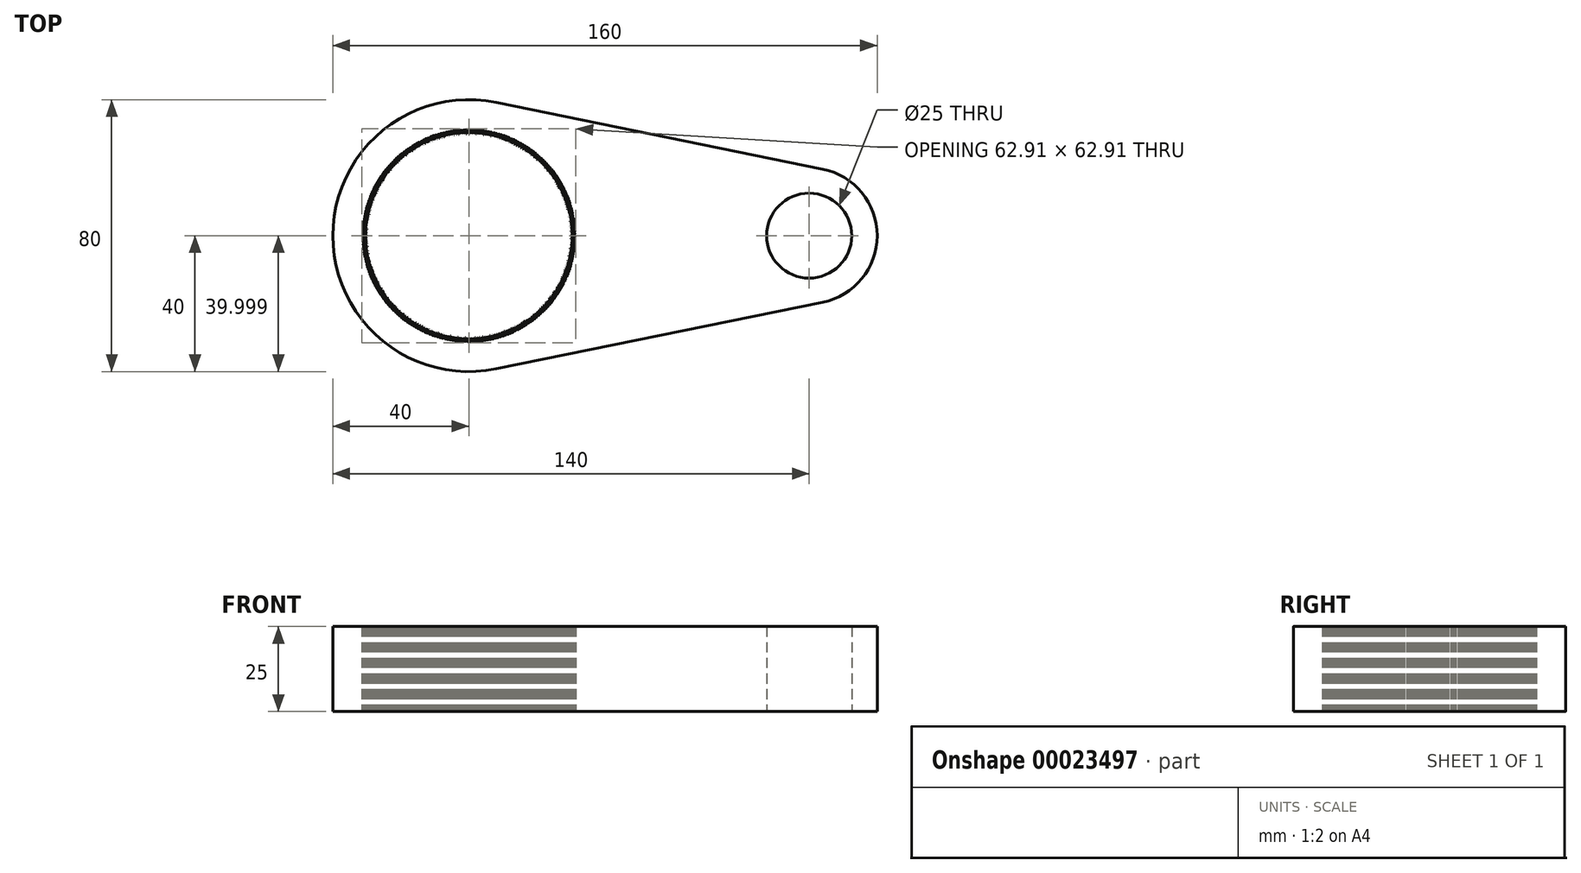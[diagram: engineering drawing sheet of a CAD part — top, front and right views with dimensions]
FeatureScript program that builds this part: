
annotation { "Feature Type Name" : "Feature", "Feature Type Description" : "" }
export const myFeature = defineFeature(function(context is Context, id is Id, definition is map)
    precondition{}
    {
        {
            var Q0;
            Q0=qCreatedBy(makeId("Top.planeOp"),FACE);
            var sketch = newSketch(context, id + "F0", { "sketchPlane" : qUnion([Q0])});
            skCircle(sketch, "E0", {"center": v(0, 0) * mm, "radius": 40 * mm});
            skCircle(sketch, "E1", {"center": v(100, 0) * mm, "radius": 20 * mm});
            skLineSegment(sketch, "E2", {"start": v(8, 39.2) * mm, "end": v(104, 19.6) * mm});
            skLineSegment(sketch, "E3", {"start": v(104, -19.6) * mm, "end": v(8, -39.2) * mm});
            skCircle(sketch, "E4", {"center": v(0, 0) * mm, "radius": 30 * mm});
            skCircle(sketch, "E5", {"center": v(100, 0) * mm, "radius": 12.5 * mm});
            skLineSegment(sketch, "E6", {"start": v(-21.76, -20.65) * mm, "end": v(-23.07, -21.39) * mm});
            skLineSegment(sketch, "E7", {"start": v(-23.07, -21.39) * mm, "end": v(-22.24, -20.14) * mm});
            skLineSegment(sketch, "E8.1.0", {"start": v(-22.25, -20.12) * mm, "end": v(-23.58, -20.82) * mm});
            skLineSegment(sketch, "E8.1.1", {"start": v(-23.58, -20.82) * mm, "end": v(-22.72, -19.6) * mm});
            skLineSegment(sketch, "E8.2.0", {"start": v(-22.74, -19.57) * mm, "end": v(-24.08, -20.24) * mm});
            skLineSegment(sketch, "E8.2.1", {"start": v(-24.08, -20.24) * mm, "end": v(-23.19, -19.04) * mm});
            skLineSegment(sketch, "E8.anchor1", {"start": v(0, 0) * mm, "end": v(-23.07, -21.39) * mm, "construction": true});
            skLineSegment(sketch, "E8.anchor2", {"start": v(0, 0) * mm, "end": v(-23.06, -21.4) * mm, "construction": true});
            skLineSegment(sketch, "E9.2.3.0", {"start": v(-23.2, -19.01) * mm, "end": v(-24.56, -19.65) * mm});
            skLineSegment(sketch, "E9.3.3.0", {"start": v(-24.56, -19.65) * mm, "end": v(-23.64, -18.47) * mm});
            skLineSegment(sketch, "E9.2.4.0", {"start": v(-23.66, -18.45) * mm, "end": v(-25.03, -19.05) * mm});
            skLineSegment(sketch, "E9.3.4.0", {"start": v(-25.03, -19.05) * mm, "end": v(-24.08, -17.89) * mm});
            skLineSegment(sketch, "E9.2.5.0", {"start": v(-24.1, -17.87) * mm, "end": v(-25.49, -18.44) * mm});
            skLineSegment(sketch, "E9.3.5.0", {"start": v(-25.49, -18.44) * mm, "end": v(-24.5, -17.3) * mm});
            skLineSegment(sketch, "E9.2.6.0", {"start": v(-24.53, -17.28) * mm, "end": v(-25.93, -17.81) * mm});
            skLineSegment(sketch, "E9.3.6.0", {"start": v(-25.93, -17.81) * mm, "end": v(-24.92, -16.7) * mm});
            skLineSegment(sketch, "E9.2.7.0", {"start": v(-24.94, -16.68) * mm, "end": v(-26.35, -17.18) * mm});
            skLineSegment(sketch, "E9.3.7.0", {"start": v(-26.35, -17.18) * mm, "end": v(-25.32, -16.1) * mm});
            skLineSegment(sketch, "E9.2.8.0", {"start": v(-25.33, -16.07) * mm, "end": v(-26.76, -16.54) * mm});
            skLineSegment(sketch, "E9.3.8.0", {"start": v(-26.76, -16.54) * mm, "end": v(-25.7, -15.47) * mm});
            skLineSegment(sketch, "E9.2.9.0", {"start": v(-25.72, -15.45) * mm, "end": v(-27.15, -15.88) * mm});
            skLineSegment(sketch, "E9.3.9.0", {"start": v(-27.15, -15.88) * mm, "end": v(-26.07, -14.84) * mm});
            skLineSegment(sketch, "E9.2.10.0", {"start": v(-26.08, -14.82) * mm, "end": v(-27.53, -15.22) * mm});
            skLineSegment(sketch, "E9.3.10.0", {"start": v(-27.53, -15.22) * mm, "end": v(-26.42, -14.2) * mm});
            skLineSegment(sketch, "E9.2.11.0", {"start": v(-26.44, -14.18) * mm, "end": v(-27.9, -14.55) * mm});
            skLineSegment(sketch, "E9.3.11.0", {"start": v(-27.9, -14.55) * mm, "end": v(-26.76, -13.56) * mm});
            skLineSegment(sketch, "E9.2.12.0", {"start": v(-26.77, -13.54) * mm, "end": v(-28.24, -13.87) * mm});
            skLineSegment(sketch, "E9.3.12.0", {"start": v(-28.24, -13.87) * mm, "end": v(-27.08, -12.9) * mm});
            skLineSegment(sketch, "E9.2.13.0", {"start": v(-27.1, -12.88) * mm, "end": v(-28.56, -13.18) * mm});
            skLineSegment(sketch, "E9.3.13.0", {"start": v(-28.56, -13.18) * mm, "end": v(-27.39, -12.25) * mm});
            skLineSegment(sketch, "E9.2.14.0", {"start": v(-27.4, -12.22) * mm, "end": v(-28.87, -12.48) * mm});
            skLineSegment(sketch, "E9.3.14.0", {"start": v(-28.87, -12.48) * mm, "end": v(-27.67, -11.58) * mm});
            skLineSegment(sketch, "E9.2.15.0", {"start": v(-27.69, -11.55) * mm, "end": v(-29.17, -11.78) * mm});
            skLineSegment(sketch, "E9.3.15.0", {"start": v(-29.17, -11.78) * mm, "end": v(-27.95, -10.9) * mm});
            skLineSegment(sketch, "E9.2.16.0", {"start": v(-27.96, -10.88) * mm, "end": v(-29.45, -11.07) * mm});
            skLineSegment(sketch, "E9.3.16.0", {"start": v(-29.45, -11.07) * mm, "end": v(-28.2, -10.23) * mm});
            skLineSegment(sketch, "E9.2.17.0", {"start": v(-28.21, -10.2) * mm, "end": v(-29.7, -10.35) * mm});
            skLineSegment(sketch, "E9.3.17.0", {"start": v(-29.7, -10.35) * mm, "end": v(-28.44, -9.54) * mm});
            skLineSegment(sketch, "E9.2.18.0", {"start": v(-28.45, -9.51) * mm, "end": v(-29.95, -9.62) * mm});
            skLineSegment(sketch, "E9.3.18.0", {"start": v(-29.95, -9.62) * mm, "end": v(-28.67, -8.85) * mm});
            skLineSegment(sketch, "E9.2.19.0", {"start": v(-28.67, -8.82) * mm, "end": v(-30.17, -8.9) * mm});
            skLineSegment(sketch, "E9.3.19.0", {"start": v(-30.17, -8.9) * mm, "end": v(-28.87, -8.15) * mm});
            skLineSegment(sketch, "E10.2.20.0", {"start": v(-28.88, -8.12) * mm, "end": v(-30.38, -8.16) * mm});
            skLineSegment(sketch, "E10.3.20.0", {"start": v(-30.38, -8.16) * mm, "end": v(-29.06, -7.44) * mm});
            skLineSegment(sketch, "E10.2.21.0", {"start": v(-29.07, -7.42) * mm, "end": v(-30.57, -7.42) * mm});
            skLineSegment(sketch, "E10.3.21.0", {"start": v(-30.57, -7.42) * mm, "end": v(-29.23, -6.74) * mm});
            skLineSegment(sketch, "E10.2.22.0", {"start": v(-29.24, -6.7) * mm, "end": v(-30.74, -6.68) * mm});
            skLineSegment(sketch, "E10.3.22.0", {"start": v(-30.74, -6.68) * mm, "end": v(-29.39, -6.03) * mm});
            skLineSegment(sketch, "E10.2.23.0", {"start": v(-29.4, -6) * mm, "end": v(-30.9, -5.93) * mm});
            skLineSegment(sketch, "E10.3.23.0", {"start": v(-30.9, -5.93) * mm, "end": v(-29.53, -5.31) * mm});
            skLineSegment(sketch, "E10.2.24.0", {"start": v(-29.53, -5.28) * mm, "end": v(-31.03, -5.18) * mm});
            skLineSegment(sketch, "E10.3.24.0", {"start": v(-31.03, -5.18) * mm, "end": v(-29.65, -4.6) * mm});
            skLineSegment(sketch, "E10.2.25.0", {"start": v(-29.65, -4.57) * mm, "end": v(-31.14, -4.42) * mm});
            skLineSegment(sketch, "E10.3.25.0", {"start": v(-31.14, -4.42) * mm, "end": v(-29.75, -3.87) * mm});
            skLineSegment(sketch, "E10.2.26.0", {"start": v(-29.75, -3.85) * mm, "end": v(-31.24, -3.67) * mm});
            skLineSegment(sketch, "E10.3.26.0", {"start": v(-31.24, -3.67) * mm, "end": v(-29.83, -3.15) * mm});
            skLineSegment(sketch, "E10.2.27.0", {"start": v(-29.84, -3.12) * mm, "end": v(-31.32, -2.9) * mm});
            skLineSegment(sketch, "E10.3.27.0", {"start": v(-31.32, -2.9) * mm, "end": v(-29.9, -2.43) * mm});
            skLineSegment(sketch, "E10.2.28.0", {"start": v(-29.9, -2.4) * mm, "end": v(-31.38, -2.15) * mm});
            skLineSegment(sketch, "E10.3.28.0", {"start": v(-31.38, -2.15) * mm, "end": v(-29.95, -1.7) * mm});
            skLineSegment(sketch, "E10.2.29.0", {"start": v(-29.95, -1.67) * mm, "end": v(-31.43, -1.39) * mm});
            skLineSegment(sketch, "E10.3.29.0", {"start": v(-31.43, -1.39) * mm, "end": v(-29.98, -0.97) * mm});
            skLineSegment(sketch, "E10.2.30.0", {"start": v(-29.99, -0.94) * mm, "end": v(-31.45, -0.62) * mm});
            skLineSegment(sketch, "E10.3.30.0", {"start": v(-31.45, -0.62) * mm, "end": v(-30, -0.25) * mm});
            skLineSegment(sketch, "E10.2.31.0", {"start": v(-30, -0.22) * mm, "end": v(-31.46, 0.14) * mm});
            skLineSegment(sketch, "E10.3.31.0", {"start": v(-31.46, 0.14) * mm, "end": v(-30, 0.48) * mm});
            skLineSegment(sketch, "E10.2.32.0", {"start": v(-30, 0.51) * mm, "end": v(-31.44, 0.9) * mm});
            skLineSegment(sketch, "E10.3.32.0", {"start": v(-31.44, 0.9) * mm, "end": v(-29.98, 1.2) * mm});
            skLineSegment(sketch, "E10.2.33.0", {"start": v(-29.97, 1.24) * mm, "end": v(-31.41, 1.66) * mm});
            skLineSegment(sketch, "E10.3.33.0", {"start": v(-31.41, 1.66) * mm, "end": v(-29.94, 1.94) * mm});
            skLineSegment(sketch, "E10.2.34.0", {"start": v(-29.94, 1.96) * mm, "end": v(-31.36, 2.43) * mm});
            skLineSegment(sketch, "E10.3.34.0", {"start": v(-31.36, 2.43) * mm, "end": v(-29.88, 2.66) * mm});
            skLineSegment(sketch, "E10.2.35.0", {"start": v(-29.88, 2.7) * mm, "end": v(-31.3, 3.19) * mm});
            skLineSegment(sketch, "E10.3.35.0", {"start": v(-31.3, 3.19) * mm, "end": v(-29.8, 3.39) * mm});
            skLineSegment(sketch, "E10.2.36.0", {"start": v(-29.8, 3.41) * mm, "end": v(-31.2, 3.94) * mm});
            skLineSegment(sketch, "E10.3.36.0", {"start": v(-31.2, 3.94) * mm, "end": v(-29.72, 4.1) * mm});
            skLineSegment(sketch, "E10.2.37.0", {"start": v(-29.71, 4.14) * mm, "end": v(-31.1, 4.7) * mm});
            skLineSegment(sketch, "E10.3.37.0", {"start": v(-31.1, 4.7) * mm, "end": v(-29.6, 4.83) * mm});
            skLineSegment(sketch, "E10.2.38.0", {"start": v(-29.6, 4.86) * mm, "end": v(-30.98, 5.45) * mm});
            skLineSegment(sketch, "E10.3.38.0", {"start": v(-30.98, 5.45) * mm, "end": v(-29.48, 5.54) * mm});
            skLineSegment(sketch, "E10.2.39.0", {"start": v(-29.48, 5.57) * mm, "end": v(-30.84, 6.2) * mm});
            skLineSegment(sketch, "E10.3.39.0", {"start": v(-30.84, 6.2) * mm, "end": v(-29.34, 6.26) * mm});
            skLineSegment(sketch, "E11.2.40.0", {"start": v(-29.33, 6.29) * mm, "end": v(-30.68, 6.95) * mm});
            skLineSegment(sketch, "E11.3.40.0", {"start": v(-30.68, 6.95) * mm, "end": v(-29.18, 6.97) * mm});
            skLineSegment(sketch, "E11.2.41.0", {"start": v(-29.17, 7) * mm, "end": v(-30.5, 7.7) * mm});
            skLineSegment(sketch, "E11.3.41.0", {"start": v(-30.5, 7.7) * mm, "end": v(-29, 7.67) * mm});
            skLineSegment(sketch, "E11.2.42.0", {"start": v(-29, 7.7) * mm, "end": v(-30.3, 8.43) * mm});
            skLineSegment(sketch, "E11.3.42.0", {"start": v(-30.3, 8.43) * mm, "end": v(-28.8, 8.37) * mm});
            skLineSegment(sketch, "E11.2.43.0", {"start": v(-28.8, 8.4) * mm, "end": v(-30.1, 9.16) * mm});
            skLineSegment(sketch, "E11.3.43.0", {"start": v(-30.1, 9.16) * mm, "end": v(-28.6, 9.07) * mm});
            skLineSegment(sketch, "E11.2.44.0", {"start": v(-28.59, 9.1) * mm, "end": v(-29.86, 9.89) * mm});
            skLineSegment(sketch, "E11.3.44.0", {"start": v(-29.86, 9.89) * mm, "end": v(-28.37, 9.76) * mm});
            skLineSegment(sketch, "E11.2.45.0", {"start": v(-28.36, 9.79) * mm, "end": v(-29.61, 10.61) * mm});
            skLineSegment(sketch, "E11.3.45.0", {"start": v(-29.61, 10.61) * mm, "end": v(-28.12, 10.45) * mm});
            skLineSegment(sketch, "E11.2.46.0", {"start": v(-28.11, 10.47) * mm, "end": v(-29.35, 11.33) * mm});
            skLineSegment(sketch, "E11.3.46.0", {"start": v(-29.35, 11.33) * mm, "end": v(-27.86, 11.13) * mm});
            skLineSegment(sketch, "E11.2.47.0", {"start": v(-27.85, 11.15) * mm, "end": v(-29.06, 12.03) * mm});
            skLineSegment(sketch, "E11.3.47.0", {"start": v(-29.06, 12.03) * mm, "end": v(-27.58, 11.8) * mm});
            skLineSegment(sketch, "E11.2.48.0", {"start": v(-27.57, 11.82) * mm, "end": v(-28.76, 12.74) * mm});
            skLineSegment(sketch, "E11.3.48.0", {"start": v(-28.76, 12.74) * mm, "end": v(-27.29, 12.46) * mm});
            skLineSegment(sketch, "E11.2.49.0", {"start": v(-27.28, 12.5) * mm, "end": v(-28.45, 13.43) * mm});
            skLineSegment(sketch, "E11.3.49.0", {"start": v(-28.45, 13.43) * mm, "end": v(-26.98, 13.12) * mm});
            skLineSegment(sketch, "E12.2.50.0", {"start": v(-26.97, 13.15) * mm, "end": v(-28.11, 14.12) * mm});
            skLineSegment(sketch, "E12.3.50.0", {"start": v(-28.11, 14.12) * mm, "end": v(-26.65, 13.77) * mm});
            skLineSegment(sketch, "E12.2.51.0", {"start": v(-26.64, 13.8) * mm, "end": v(-27.76, 14.8) * mm});
            skLineSegment(sketch, "E12.3.51.0", {"start": v(-27.76, 14.8) * mm, "end": v(-26.3, 14.42) * mm});
            skLineSegment(sketch, "E12.2.52.0", {"start": v(-26.3, 14.44) * mm, "end": v(-27.4, 15.46) * mm});
            skLineSegment(sketch, "E12.3.52.0", {"start": v(-27.4, 15.46) * mm, "end": v(-25.95, 15.05) * mm});
            skLineSegment(sketch, "E12.2.53.0", {"start": v(-25.94, 15.07) * mm, "end": v(-27.01, 16.12) * mm});
            skLineSegment(sketch, "E12.3.53.0", {"start": v(-27.01, 16.12) * mm, "end": v(-25.58, 15.67) * mm});
            skLineSegment(sketch, "E12.2.54.0", {"start": v(-25.56, 15.7) * mm, "end": v(-26.61, 16.77) * mm});
            skLineSegment(sketch, "E12.3.54.0", {"start": v(-26.61, 16.77) * mm, "end": v(-25.2, 16.3) * mm});
            skLineSegment(sketch, "E12.2.55.0", {"start": v(-25.18, 16.31) * mm, "end": v(-26.2, 17.41) * mm});
            skLineSegment(sketch, "E12.3.55.0", {"start": v(-26.2, 17.41) * mm, "end": v(-24.79, 16.9) * mm});
            skLineSegment(sketch, "E12.2.56.0", {"start": v(-24.77, 16.92) * mm, "end": v(-25.77, 18.04) * mm});
            skLineSegment(sketch, "E12.3.56.0", {"start": v(-25.77, 18.04) * mm, "end": v(-24.37, 17.5) * mm});
            skLineSegment(sketch, "E12.2.57.0", {"start": v(-24.36, 17.52) * mm, "end": v(-25.32, 18.66) * mm});
            skLineSegment(sketch, "E12.3.57.0", {"start": v(-25.32, 18.66) * mm, "end": v(-23.94, 18.08) * mm});
            skLineSegment(sketch, "E12.2.58.0", {"start": v(-23.92, 18.1) * mm, "end": v(-24.86, 19.27) * mm});
            skLineSegment(sketch, "E12.3.58.0", {"start": v(-24.86, 19.27) * mm, "end": v(-23.5, 18.65) * mm});
            skLineSegment(sketch, "E12.2.59.0", {"start": v(-23.48, 18.68) * mm, "end": v(-24.39, 19.87) * mm});
            skLineSegment(sketch, "E12.3.59.0", {"start": v(-24.39, 19.87) * mm, "end": v(-23.04, 19.22) * mm});
            skLineSegment(sketch, "E13.2.60.0", {"start": v(-23.02, 19.24) * mm, "end": v(-23.9, 20.45) * mm});
            skLineSegment(sketch, "E13.3.60.0", {"start": v(-23.9, 20.45) * mm, "end": v(-22.56, 19.77) * mm});
            skLineSegment(sketch, "E13.2.61.0", {"start": v(-22.54, 19.8) * mm, "end": v(-23.4, 21.03) * mm});
            skLineSegment(sketch, "E13.3.61.0", {"start": v(-23.4, 21.03) * mm, "end": v(-22.08, 20.31) * mm});
            skLineSegment(sketch, "E13.2.62.0", {"start": v(-22.06, 20.33) * mm, "end": v(-22.88, 21.59) * mm});
            skLineSegment(sketch, "E13.3.62.0", {"start": v(-22.88, 21.59) * mm, "end": v(-21.58, 20.84) * mm});
            skLineSegment(sketch, "E13.2.63.0", {"start": v(-21.56, 20.86) * mm, "end": v(-22.35, 22.14) * mm});
            skLineSegment(sketch, "E13.3.63.0", {"start": v(-22.35, 22.14) * mm, "end": v(-21.07, 21.36) * mm});
            skLineSegment(sketch, "E13.2.64.0", {"start": v(-21.05, 21.38) * mm, "end": v(-21.8, 22.67) * mm});
            skLineSegment(sketch, "E13.3.64.0", {"start": v(-21.8, 22.67) * mm, "end": v(-20.54, 21.86) * mm});
            skLineSegment(sketch, "E13.2.65.0", {"start": v(-20.52, 21.88) * mm, "end": v(-21.25, 23.2) * mm});
            skLineSegment(sketch, "E13.3.65.0", {"start": v(-21.25, 23.2) * mm, "end": v(-20, 22.36) * mm});
            skLineSegment(sketch, "E13.2.66.0", {"start": v(-19.98, 22.38) * mm, "end": v(-20.68, 23.7) * mm});
            skLineSegment(sketch, "E13.3.66.0", {"start": v(-20.68, 23.7) * mm, "end": v(-19.46, 22.84) * mm});
            skLineSegment(sketch, "E13.2.67.0", {"start": v(-19.43, 22.85) * mm, "end": v(-20.1, 24.2) * mm});
            skLineSegment(sketch, "E13.3.67.0", {"start": v(-20.1, 24.2) * mm, "end": v(-18.9, 23.3) * mm});
            skLineSegment(sketch, "E13.2.68.0", {"start": v(-18.87, 23.32) * mm, "end": v(-19.5, 24.68) * mm});
            skLineSegment(sketch, "E13.3.68.0", {"start": v(-19.5, 24.68) * mm, "end": v(-18.33, 23.75) * mm});
            skLineSegment(sketch, "E13.2.69.0", {"start": v(-18.3, 23.77) * mm, "end": v(-18.9, 25.15) * mm});
            skLineSegment(sketch, "E13.3.69.0", {"start": v(-18.9, 25.15) * mm, "end": v(-17.74, 24.19) * mm});
            skLineSegment(sketch, "E14.2.70.0", {"start": v(-17.72, 24.2) * mm, "end": v(-18.28, 25.6) * mm});
            skLineSegment(sketch, "E14.3.70.0", {"start": v(-18.28, 25.6) * mm, "end": v(-17.15, 24.61) * mm});
            skLineSegment(sketch, "E14.2.71.0", {"start": v(-17.13, 24.63) * mm, "end": v(-17.66, 26.03) * mm});
            skLineSegment(sketch, "E14.3.71.0", {"start": v(-17.66, 26.03) * mm, "end": v(-16.55, 25.02) * mm});
            skLineSegment(sketch, "E14.2.72.0", {"start": v(-16.53, 25.04) * mm, "end": v(-17.02, 26.45) * mm});
            skLineSegment(sketch, "E14.3.72.0", {"start": v(-17.02, 26.45) * mm, "end": v(-15.94, 25.42) * mm});
            skLineSegment(sketch, "E14.2.73.0", {"start": v(-15.91, 25.43) * mm, "end": v(-16.38, 26.86) * mm});
            skLineSegment(sketch, "E14.3.73.0", {"start": v(-16.38, 26.86) * mm, "end": v(-15.32, 25.8) * mm});
            skLineSegment(sketch, "E14.2.74.0", {"start": v(-15.3, 25.8) * mm, "end": v(-15.72, 27.25) * mm});
            skLineSegment(sketch, "E14.3.74.0", {"start": v(-15.72, 27.25) * mm, "end": v(-14.69, 26.16) * mm});
            skLineSegment(sketch, "E14.2.75.0", {"start": v(-14.66, 26.17) * mm, "end": v(-15.05, 27.62) * mm});
            skLineSegment(sketch, "E14.3.75.0", {"start": v(-15.05, 27.62) * mm, "end": v(-14.05, 26.5) * mm});
            skLineSegment(sketch, "E14.2.76.0", {"start": v(-14.02, 26.52) * mm, "end": v(-14.38, 27.98) * mm});
            skLineSegment(sketch, "E14.3.76.0", {"start": v(-14.38, 27.98) * mm, "end": v(-13.4, 26.84) * mm});
            skLineSegment(sketch, "E14.2.77.0", {"start": v(-13.38, 26.85) * mm, "end": v(-13.7, 28.32) * mm});
            skLineSegment(sketch, "E14.3.77.0", {"start": v(-13.7, 28.32) * mm, "end": v(-12.75, 27.16) * mm});
            skLineSegment(sketch, "E14.2.78.0", {"start": v(-12.72, 27.17) * mm, "end": v(-13, 28.64) * mm});
            skLineSegment(sketch, "E14.3.78.0", {"start": v(-13, 28.64) * mm, "end": v(-12.08, 27.46) * mm});
            skLineSegment(sketch, "E14.2.79.0", {"start": v(-12.06, 27.47) * mm, "end": v(-12.3, 28.95) * mm});
            skLineSegment(sketch, "E14.3.79.0", {"start": v(-12.3, 28.95) * mm, "end": v(-11.41, 27.74) * mm});
            skLineSegment(sketch, "E15.2.80.0", {"start": v(-11.39, 27.75) * mm, "end": v(-11.6, 29.24) * mm});
            skLineSegment(sketch, "E15.3.80.0", {"start": v(-11.6, 29.24) * mm, "end": v(-10.74, 28.01) * mm});
            skLineSegment(sketch, "E15.2.81.0", {"start": v(-10.71, 28.02) * mm, "end": v(-10.89, 29.51) * mm});
            skLineSegment(sketch, "E15.3.81.0", {"start": v(-10.89, 29.51) * mm, "end": v(-10.06, 28.26) * mm});
            skLineSegment(sketch, "E15.2.82.0", {"start": v(-10.03, 28.27) * mm, "end": v(-10.17, 29.77) * mm});
            skLineSegment(sketch, "E15.3.82.0", {"start": v(-10.17, 29.77) * mm, "end": v(-9.37, 28.5) * mm});
            skLineSegment(sketch, "E15.2.83.0", {"start": v(-9.34, 28.5) * mm, "end": v(-9.44, 30) * mm});
            skLineSegment(sketch, "E15.3.83.0", {"start": v(-9.44, 30) * mm, "end": v(-8.67, 28.72) * mm});
            skLineSegment(sketch, "E15.2.84.0", {"start": v(-8.65, 28.73) * mm, "end": v(-8.71, 30.23) * mm});
            skLineSegment(sketch, "E15.3.84.0", {"start": v(-8.71, 30.23) * mm, "end": v(-7.97, 28.92) * mm});
            skLineSegment(sketch, "E15.2.85.0", {"start": v(-7.95, 28.93) * mm, "end": v(-7.98, 30.43) * mm});
            skLineSegment(sketch, "E15.3.85.0", {"start": v(-7.98, 30.43) * mm, "end": v(-7.27, 29.1) * mm});
            skLineSegment(sketch, "E15.2.86.0", {"start": v(-7.24, 29.11) * mm, "end": v(-7.24, 30.61) * mm});
            skLineSegment(sketch, "E15.3.86.0", {"start": v(-7.24, 30.61) * mm, "end": v(-6.56, 29.27) * mm});
            skLineSegment(sketch, "E15.2.87.0", {"start": v(-6.53, 29.28) * mm, "end": v(-6.5, 30.78) * mm});
            skLineSegment(sketch, "E15.3.87.0", {"start": v(-6.5, 30.78) * mm, "end": v(-5.85, 29.42) * mm});
            skLineSegment(sketch, "E15.2.88.0", {"start": v(-5.82, 29.43) * mm, "end": v(-5.74, 30.93) * mm});
            skLineSegment(sketch, "E15.3.88.0", {"start": v(-5.74, 30.93) * mm, "end": v(-5.13, 29.56) * mm});
            skLineSegment(sketch, "E15.2.89.0", {"start": v(-5.1, 29.56) * mm, "end": v(-5, 31.06) * mm});
            skLineSegment(sketch, "E15.3.89.0", {"start": v(-5, 31.06) * mm, "end": v(-4.42, 29.67) * mm});
            skLineSegment(sketch, "E15.2.90.0", {"start": v(-4.39, 29.68) * mm, "end": v(-4.24, 31.17) * mm});
            skLineSegment(sketch, "E15.3.90.0", {"start": v(-4.24, 31.17) * mm, "end": v(-3.7, 29.77) * mm});
            skLineSegment(sketch, "E15.2.91.0", {"start": v(-3.67, 29.78) * mm, "end": v(-3.48, 31.26) * mm});
            skLineSegment(sketch, "E15.3.91.0", {"start": v(-3.48, 31.26) * mm, "end": v(-2.97, 29.85) * mm});
            skLineSegment(sketch, "E15.2.92.0", {"start": v(-2.94, 29.86) * mm, "end": v(-2.72, 31.34) * mm});
            skLineSegment(sketch, "E15.3.92.0", {"start": v(-2.72, 31.34) * mm, "end": v(-2.25, 29.92) * mm});
            skLineSegment(sketch, "E15.2.93.0", {"start": v(-2.22, 29.92) * mm, "end": v(-1.96, 31.4) * mm});
            skLineSegment(sketch, "E15.3.93.0", {"start": v(-1.96, 31.4) * mm, "end": v(-1.52, 29.96) * mm});
            skLineSegment(sketch, "E15.2.94.0", {"start": v(-1.5, 29.96) * mm, "end": v(-1.2, 31.43) * mm});
            skLineSegment(sketch, "E15.3.94.0", {"start": v(-1.2, 31.43) * mm, "end": v(-0.8, 29.99) * mm});
            skLineSegment(sketch, "E15.2.95.0", {"start": v(-0.76, 30) * mm, "end": v(-0.43, 31.45) * mm});
            skLineSegment(sketch, "E15.3.95.0", {"start": v(-0.43, 31.45) * mm, "end": v(-0.06, 30) * mm});
            skLineSegment(sketch, "E15.2.96.0", {"start": v(-0.04, 30) * mm, "end": v(0.33, 31.45) * mm});
            skLineSegment(sketch, "E15.3.96.0", {"start": v(0.33, 31.45) * mm, "end": v(0.66, 30) * mm});
            skLineSegment(sketch, "E15.2.97.0", {"start": v(0.7, 30) * mm, "end": v(1.1, 31.44) * mm});
            skLineSegment(sketch, "E15.3.97.0", {"start": v(1.1, 31.44) * mm, "end": v(1.4, 29.97) * mm});
            skLineSegment(sketch, "E15.2.98.0", {"start": v(1.42, 29.97) * mm, "end": v(1.85, 31.4) * mm});
            skLineSegment(sketch, "E15.3.98.0", {"start": v(1.85, 31.4) * mm, "end": v(2.12, 29.93) * mm});
            skLineSegment(sketch, "E15.2.99.0", {"start": v(2.14, 29.92) * mm, "end": v(2.61, 31.35) * mm});
            skLineSegment(sketch, "E15.3.99.0", {"start": v(2.61, 31.35) * mm, "end": v(2.84, 29.87) * mm});
            skLineSegment(sketch, "E16.2.100.0", {"start": v(2.87, 29.86) * mm, "end": v(3.37, 31.28) * mm});
            skLineSegment(sketch, "E16.3.100.0", {"start": v(3.37, 31.28) * mm, "end": v(3.57, 29.79) * mm});
            skLineSegment(sketch, "E16.2.101.0", {"start": v(3.6, 29.78) * mm, "end": v(4.13, 31.18) * mm});
            skLineSegment(sketch, "E16.3.101.0", {"start": v(4.13, 31.18) * mm, "end": v(4.29, 29.7) * mm});
            skLineSegment(sketch, "E16.2.102.0", {"start": v(4.31, 29.69) * mm, "end": v(4.89, 31.07) * mm});
            skLineSegment(sketch, "E16.3.102.0", {"start": v(4.89, 31.07) * mm, "end": v(5, 29.58) * mm});
            skLineSegment(sketch, "E16.2.103.0", {"start": v(5.03, 29.57) * mm, "end": v(5.64, 30.95) * mm});
            skLineSegment(sketch, "E16.3.103.0", {"start": v(5.64, 30.95) * mm, "end": v(5.72, 29.45) * mm});
            skLineSegment(sketch, "E16.2.104.0", {"start": v(5.75, 29.44) * mm, "end": v(6.39, 30.8) * mm});
            skLineSegment(sketch, "E16.3.104.0", {"start": v(6.39, 30.8) * mm, "end": v(6.43, 29.3) * mm});
            skLineSegment(sketch, "E16.2.105.0", {"start": v(6.46, 29.3) * mm, "end": v(7.13, 30.64) * mm});
            skLineSegment(sketch, "E16.3.105.0", {"start": v(7.13, 30.64) * mm, "end": v(7.14, 29.14) * mm});
            skLineSegment(sketch, "E16.2.106.0", {"start": v(7.17, 29.13) * mm, "end": v(7.87, 30.46) * mm});
            skLineSegment(sketch, "E16.3.106.0", {"start": v(7.87, 30.46) * mm, "end": v(7.85, 28.96) * mm});
            skLineSegment(sketch, "E16.2.107.0", {"start": v(7.88, 28.95) * mm, "end": v(8.61, 30.26) * mm});
            skLineSegment(sketch, "E16.3.107.0", {"start": v(8.61, 30.26) * mm, "end": v(8.55, 28.76) * mm});
            skLineSegment(sketch, "E16.2.108.0", {"start": v(8.58, 28.75) * mm, "end": v(9.34, 30.04) * mm});
            skLineSegment(sketch, "E16.3.108.0", {"start": v(9.34, 30.04) * mm, "end": v(9.24, 28.54) * mm});
            skLineSegment(sketch, "E16.2.109.0", {"start": v(9.27, 28.53) * mm, "end": v(10.07, 29.8) * mm});
            skLineSegment(sketch, "E16.3.109.0", {"start": v(10.07, 29.8) * mm, "end": v(9.93, 28.3) * mm});
            skLineSegment(sketch, "E16.2.110.0", {"start": v(9.96, 28.3) * mm, "end": v(10.79, 29.55) * mm});
            skLineSegment(sketch, "E16.3.110.0", {"start": v(10.79, 29.55) * mm, "end": v(10.62, 28.06) * mm});
            skLineSegment(sketch, "E16.2.111.0", {"start": v(10.64, 28.05) * mm, "end": v(11.5, 29.28) * mm});
            skLineSegment(sketch, "E16.3.111.0", {"start": v(11.5, 29.28) * mm, "end": v(11.3, 27.8) * mm});
            skLineSegment(sketch, "E16.2.112.0", {"start": v(11.32, 27.78) * mm, "end": v(12.2, 29) * mm});
            skLineSegment(sketch, "E16.3.112.0", {"start": v(12.2, 29) * mm, "end": v(11.96, 27.51) * mm});
            skLineSegment(sketch, "E16.2.113.0", {"start": v(12, 27.5) * mm, "end": v(12.9, 28.69) * mm});
            skLineSegment(sketch, "E16.3.113.0", {"start": v(12.9, 28.69) * mm, "end": v(12.63, 27.21) * mm});
            skLineSegment(sketch, "E16.2.114.0", {"start": v(12.65, 27.2) * mm, "end": v(13.6, 28.36) * mm});
            skLineSegment(sketch, "E16.3.114.0", {"start": v(13.6, 28.36) * mm, "end": v(13.28, 26.9) * mm});
            skLineSegment(sketch, "E16.2.115.0", {"start": v(13.31, 26.89) * mm, "end": v(14.28, 28.03) * mm});
            skLineSegment(sketch, "E16.3.115.0", {"start": v(14.28, 28.03) * mm, "end": v(13.93, 26.57) * mm});
            skLineSegment(sketch, "E16.2.116.0", {"start": v(13.96, 26.55) * mm, "end": v(14.96, 27.67) * mm});
            skLineSegment(sketch, "E16.3.116.0", {"start": v(14.96, 27.67) * mm, "end": v(14.57, 26.22) * mm});
            skLineSegment(sketch, "E16.2.117.0", {"start": v(14.6, 26.2) * mm, "end": v(15.63, 27.3) * mm});
            skLineSegment(sketch, "E16.3.117.0", {"start": v(15.63, 27.3) * mm, "end": v(15.2, 25.86) * mm});
            skLineSegment(sketch, "E16.2.118.0", {"start": v(15.23, 25.85) * mm, "end": v(16.28, 26.91) * mm});
            skLineSegment(sketch, "E16.3.118.0", {"start": v(16.28, 26.91) * mm, "end": v(15.83, 25.48) * mm});
            skLineSegment(sketch, "E16.2.119.0", {"start": v(15.85, 25.47) * mm, "end": v(16.93, 26.51) * mm});
            skLineSegment(sketch, "E16.3.119.0", {"start": v(16.93, 26.51) * mm, "end": v(16.44, 25.1) * mm});
            skLineSegment(sketch, "E17.2.120.0", {"start": v(16.47, 25.08) * mm, "end": v(17.57, 26.1) * mm});
            skLineSegment(sketch, "E17.3.120.0", {"start": v(17.57, 26.1) * mm, "end": v(17.05, 24.69) * mm});
            skLineSegment(sketch, "E17.2.121.0", {"start": v(17.07, 24.67) * mm, "end": v(18.2, 25.66) * mm});
            skLineSegment(sketch, "E17.3.121.0", {"start": v(18.2, 25.66) * mm, "end": v(17.64, 24.27) * mm});
            skLineSegment(sketch, "E17.2.122.0", {"start": v(17.66, 24.25) * mm, "end": v(18.82, 25.2) * mm});
            skLineSegment(sketch, "E17.3.122.0", {"start": v(18.82, 25.2) * mm, "end": v(18.22, 23.83) * mm});
            skLineSegment(sketch, "E17.2.123.0", {"start": v(18.25, 23.81) * mm, "end": v(19.42, 24.75) * mm});
            skLineSegment(sketch, "E17.3.123.0", {"start": v(19.42, 24.75) * mm, "end": v(18.8, 23.38) * mm});
            skLineSegment(sketch, "E17.2.124.0", {"start": v(18.82, 23.36) * mm, "end": v(20.02, 24.27) * mm});
            skLineSegment(sketch, "E17.3.124.0", {"start": v(20.02, 24.27) * mm, "end": v(19.36, 22.92) * mm});
            skLineSegment(sketch, "E17.2.125.0", {"start": v(19.38, 22.9) * mm, "end": v(20.6, 23.77) * mm});
            skLineSegment(sketch, "E17.3.125.0", {"start": v(20.6, 23.77) * mm, "end": v(19.9, 22.44) * mm});
            skLineSegment(sketch, "E17.2.126.0", {"start": v(19.93, 22.42) * mm, "end": v(21.17, 23.27) * mm});
            skLineSegment(sketch, "E17.3.126.0", {"start": v(21.17, 23.27) * mm, "end": v(20.45, 21.95) * mm});
            skLineSegment(sketch, "E17.2.127.0", {"start": v(20.47, 21.93) * mm, "end": v(21.73, 22.75) * mm});
            skLineSegment(sketch, "E17.3.127.0", {"start": v(21.73, 22.75) * mm, "end": v(20.97, 21.45) * mm});
            skLineSegment(sketch, "E17.2.128.0", {"start": v(21, 21.43) * mm, "end": v(22.27, 22.21) * mm});
            skLineSegment(sketch, "E17.3.128.0", {"start": v(22.27, 22.21) * mm, "end": v(21.49, 20.94) * mm});
            skLineSegment(sketch, "E17.2.129.0", {"start": v(21.5, 20.92) * mm, "end": v(22.8, 21.67) * mm});
            skLineSegment(sketch, "E17.3.129.0", {"start": v(22.8, 21.67) * mm, "end": v(21.99, 20.4) * mm});
            skLineSegment(sketch, "E17.2.130.0", {"start": v(22, 20.39) * mm, "end": v(23.32, 21.1) * mm});
            skLineSegment(sketch, "E17.3.130.0", {"start": v(23.32, 21.1) * mm, "end": v(22.48, 19.87) * mm});
            skLineSegment(sketch, "E17.2.131.0", {"start": v(22.5, 19.85) * mm, "end": v(23.83, 20.54) * mm});
            skLineSegment(sketch, "E17.3.131.0", {"start": v(23.83, 20.54) * mm, "end": v(22.95, 19.32) * mm});
            skLineSegment(sketch, "E17.2.132.0", {"start": v(22.97, 19.3) * mm, "end": v(24.32, 19.95) * mm});
            skLineSegment(sketch, "E17.3.132.0", {"start": v(24.32, 19.95) * mm, "end": v(23.41, 18.76) * mm});
            skLineSegment(sketch, "E17.2.133.0", {"start": v(23.43, 18.73) * mm, "end": v(24.8, 19.36) * mm});
            skLineSegment(sketch, "E17.3.133.0", {"start": v(24.8, 19.36) * mm, "end": v(23.86, 18.18) * mm});
            skLineSegment(sketch, "E17.2.134.0", {"start": v(23.88, 18.16) * mm, "end": v(25.26, 18.75) * mm});
            skLineSegment(sketch, "E17.3.134.0", {"start": v(25.26, 18.75) * mm, "end": v(24.3, 17.6) * mm});
            skLineSegment(sketch, "E17.2.135.0", {"start": v(24.31, 17.58) * mm, "end": v(25.7, 18.13) * mm});
            skLineSegment(sketch, "E17.3.135.0", {"start": v(25.7, 18.13) * mm, "end": v(24.72, 17) * mm});
            skLineSegment(sketch, "E17.2.136.0", {"start": v(24.73, 16.98) * mm, "end": v(26.14, 17.5) * mm});
            skLineSegment(sketch, "E17.3.136.0", {"start": v(26.14, 17.5) * mm, "end": v(25.12, 16.4) * mm});
            skLineSegment(sketch, "E17.2.137.0", {"start": v(25.14, 16.38) * mm, "end": v(26.56, 16.86) * mm});
            skLineSegment(sketch, "E17.3.137.0", {"start": v(26.56, 16.86) * mm, "end": v(25.51, 15.79) * mm});
            skLineSegment(sketch, "E17.2.138.0", {"start": v(25.53, 15.76) * mm, "end": v(26.96, 16.21) * mm});
            skLineSegment(sketch, "E17.3.138.0", {"start": v(26.96, 16.21) * mm, "end": v(25.89, 15.16) * mm});
            skLineSegment(sketch, "E17.2.139.0", {"start": v(25.9, 15.14) * mm, "end": v(27.34, 15.55) * mm});
            skLineSegment(sketch, "E17.3.139.0", {"start": v(27.34, 15.55) * mm, "end": v(26.25, 14.53) * mm});
            skLineSegment(sketch, "E17.2.140.0", {"start": v(26.26, 14.5) * mm, "end": v(27.71, 14.89) * mm});
            skLineSegment(sketch, "E17.3.140.0", {"start": v(27.71, 14.89) * mm, "end": v(26.6, 13.89) * mm});
            skLineSegment(sketch, "E17.2.141.0", {"start": v(26.6, 13.86) * mm, "end": v(28.06, 14.21) * mm});
            skLineSegment(sketch, "E17.3.141.0", {"start": v(28.06, 14.21) * mm, "end": v(26.92, 13.24) * mm});
            skLineSegment(sketch, "E17.2.142.0", {"start": v(26.93, 13.21) * mm, "end": v(28.4, 13.53) * mm});
            skLineSegment(sketch, "E17.3.142.0", {"start": v(28.4, 13.53) * mm, "end": v(27.23, 12.58) * mm});
            skLineSegment(sketch, "E17.2.143.0", {"start": v(27.25, 12.56) * mm, "end": v(28.72, 12.83) * mm});
            skLineSegment(sketch, "E17.3.143.0", {"start": v(28.72, 12.83) * mm, "end": v(27.53, 11.92) * mm});
            skLineSegment(sketch, "E17.2.144.0", {"start": v(27.54, 11.9) * mm, "end": v(29.02, 12.13) * mm});
            skLineSegment(sketch, "E17.3.144.0", {"start": v(29.02, 12.13) * mm, "end": v(27.81, 11.25) * mm});
            skLineSegment(sketch, "E17.2.145.0", {"start": v(27.82, 11.22) * mm, "end": v(29.3, 11.42) * mm});
            skLineSegment(sketch, "E17.3.145.0", {"start": v(29.3, 11.42) * mm, "end": v(28.08, 10.57) * mm});
            skLineSegment(sketch, "E17.2.146.0", {"start": v(28.09, 10.54) * mm, "end": v(29.58, 10.71) * mm});
            skLineSegment(sketch, "E17.3.146.0", {"start": v(29.58, 10.71) * mm, "end": v(28.32, 9.88) * mm});
            skLineSegment(sketch, "E17.2.147.0", {"start": v(28.33, 9.86) * mm, "end": v(29.83, 9.99) * mm});
            skLineSegment(sketch, "E17.3.147.0", {"start": v(29.83, 9.99) * mm, "end": v(28.56, 9.2) * mm});
            skLineSegment(sketch, "E17.2.148.0", {"start": v(28.56, 9.17) * mm, "end": v(30.06, 9.26) * mm});
            skLineSegment(sketch, "E17.3.148.0", {"start": v(30.06, 9.26) * mm, "end": v(28.77, 8.5) * mm});
            skLineSegment(sketch, "E17.2.149.0", {"start": v(28.78, 8.47) * mm, "end": v(30.28, 8.53) * mm});
            skLineSegment(sketch, "E17.3.149.0", {"start": v(30.28, 8.53) * mm, "end": v(28.97, 7.8) * mm});
            skLineSegment(sketch, "E18.2.150.0", {"start": v(28.98, 7.77) * mm, "end": v(30.48, 7.8) * mm});
            skLineSegment(sketch, "E18.3.150.0", {"start": v(30.48, 7.8) * mm, "end": v(29.15, 7.1) * mm});
            skLineSegment(sketch, "E18.2.151.0", {"start": v(29.16, 7.07) * mm, "end": v(30.66, 7.05) * mm});
            skLineSegment(sketch, "E18.3.151.0", {"start": v(30.66, 7.05) * mm, "end": v(29.31, 6.38) * mm});
            skLineSegment(sketch, "E18.2.152.0", {"start": v(29.32, 6.36) * mm, "end": v(30.82, 6.3) * mm});
            skLineSegment(sketch, "E18.3.152.0", {"start": v(30.82, 6.3) * mm, "end": v(29.46, 5.67) * mm});
            skLineSegment(sketch, "E18.2.153.0", {"start": v(29.46, 5.64) * mm, "end": v(30.96, 5.56) * mm});
            skLineSegment(sketch, "E18.3.153.0", {"start": v(30.96, 5.56) * mm, "end": v(29.59, 4.96) * mm});
            skLineSegment(sketch, "E18.2.154.0", {"start": v(29.6, 4.93) * mm, "end": v(31.09, 4.8) * mm});
            skLineSegment(sketch, "E18.3.154.0", {"start": v(31.09, 4.8) * mm, "end": v(29.7, 4.24) * mm});
            skLineSegment(sketch, "E18.2.155.0", {"start": v(29.7, 4.2) * mm, "end": v(31.2, 4.05) * mm});
            skLineSegment(sketch, "E18.3.155.0", {"start": v(31.2, 4.05) * mm, "end": v(29.8, 3.51) * mm});
            skLineSegment(sketch, "E18.2.156.0", {"start": v(29.8, 3.49) * mm, "end": v(31.28, 3.3) * mm});
            skLineSegment(sketch, "E18.3.156.0", {"start": v(31.28, 3.3) * mm, "end": v(29.87, 2.8) * mm});
            skLineSegment(sketch, "E18.2.157.0", {"start": v(29.87, 2.76) * mm, "end": v(31.35, 2.53) * mm});
            skLineSegment(sketch, "E18.3.157.0", {"start": v(31.35, 2.53) * mm, "end": v(29.93, 2.07) * mm});
            skLineSegment(sketch, "E18.2.158.0", {"start": v(29.93, 2.04) * mm, "end": v(31.4, 1.77) * mm});
            skLineSegment(sketch, "E18.3.158.0", {"start": v(31.4, 1.77) * mm, "end": v(29.97, 1.34) * mm});
            skLineSegment(sketch, "E18.2.159.0", {"start": v(29.97, 1.31) * mm, "end": v(31.44, 1) * mm});
            skLineSegment(sketch, "E18.3.159.0", {"start": v(31.44, 1) * mm, "end": v(30, 0.61) * mm});
            skLineSegment(sketch, "E18.2.160.0", {"start": v(30, 0.58) * mm, "end": v(31.46, 0.25) * mm});
            skLineSegment(sketch, "E18.3.160.0", {"start": v(31.46, 0.25) * mm, "end": v(30, -0.12) * mm});
            skLineSegment(sketch, "E18.2.161.0", {"start": v(30, -0.14) * mm, "end": v(31.45, -0.52) * mm});
            skLineSegment(sketch, "E18.3.161.0", {"start": v(31.45, -0.52) * mm, "end": v(29.99, -0.84) * mm});
            skLineSegment(sketch, "E18.2.162.0", {"start": v(29.99, -0.87) * mm, "end": v(31.43, -1.28) * mm});
            skLineSegment(sketch, "E18.3.162.0", {"start": v(31.43, -1.28) * mm, "end": v(29.96, -1.57) * mm});
            skLineSegment(sketch, "E18.2.163.0", {"start": v(29.96, -1.6) * mm, "end": v(31.4, -2.04) * mm});
            skLineSegment(sketch, "E18.3.163.0", {"start": v(31.4, -2.04) * mm, "end": v(29.91, -2.3) * mm});
            skLineSegment(sketch, "E18.2.164.0", {"start": v(29.9, -2.32) * mm, "end": v(31.33, -2.8) * mm});
            skLineSegment(sketch, "E18.3.164.0", {"start": v(31.33, -2.8) * mm, "end": v(29.85, -3.02) * mm});
            skLineSegment(sketch, "E18.2.165.0", {"start": v(29.84, -3.05) * mm, "end": v(31.25, -3.56) * mm});
            skLineSegment(sketch, "E18.3.165.0", {"start": v(31.25, -3.56) * mm, "end": v(29.77, -3.74) * mm});
            skLineSegment(sketch, "E18.2.166.0", {"start": v(29.76, -3.77) * mm, "end": v(31.16, -4.32) * mm});
            skLineSegment(sketch, "E18.3.166.0", {"start": v(31.16, -4.32) * mm, "end": v(29.67, -4.47) * mm});
            skLineSegment(sketch, "E18.2.167.0", {"start": v(29.66, -4.5) * mm, "end": v(31.04, -5.07) * mm});
            skLineSegment(sketch, "E18.3.167.0", {"start": v(31.04, -5.07) * mm, "end": v(29.55, -5.18) * mm});
            skLineSegment(sketch, "E18.2.168.0", {"start": v(29.54, -5.21) * mm, "end": v(30.91, -5.83) * mm});
            skLineSegment(sketch, "E18.3.168.0", {"start": v(30.91, -5.83) * mm, "end": v(29.41, -5.9) * mm});
            skLineSegment(sketch, "E18.2.169.0", {"start": v(29.4, -5.93) * mm, "end": v(30.76, -6.57) * mm});
            skLineSegment(sketch, "E18.3.169.0", {"start": v(30.76, -6.57) * mm, "end": v(29.26, -6.61) * mm});
            skLineSegment(sketch, "E18.2.170.0", {"start": v(29.26, -6.64) * mm, "end": v(30.6, -7.32) * mm});
            skLineSegment(sketch, "E18.3.170.0", {"start": v(30.6, -7.32) * mm, "end": v(29.1, -7.32) * mm});
            skLineSegment(sketch, "E18.2.171.0", {"start": v(29.09, -7.35) * mm, "end": v(30.4, -8.06) * mm});
            skLineSegment(sketch, "E18.3.171.0", {"start": v(30.4, -8.06) * mm, "end": v(28.9, -8.02) * mm});
            skLineSegment(sketch, "E18.2.172.0", {"start": v(28.9, -8.05) * mm, "end": v(30.2, -8.8) * mm});
            skLineSegment(sketch, "E18.3.172.0", {"start": v(30.2, -8.8) * mm, "end": v(28.7, -8.72) * mm});
            skLineSegment(sketch, "E18.2.173.0", {"start": v(28.7, -8.75) * mm, "end": v(29.98, -9.52) * mm});
            skLineSegment(sketch, "E18.3.173.0", {"start": v(29.98, -9.52) * mm, "end": v(28.48, -9.41) * mm});
            skLineSegment(sketch, "E18.2.174.0", {"start": v(28.48, -9.44) * mm, "end": v(29.74, -10.25) * mm});
            skLineSegment(sketch, "E18.3.174.0", {"start": v(29.74, -10.25) * mm, "end": v(28.25, -10.1) * mm});
            skLineSegment(sketch, "E18.2.175.0", {"start": v(28.24, -10.13) * mm, "end": v(29.48, -10.97) * mm});
            skLineSegment(sketch, "E18.3.175.0", {"start": v(29.48, -10.97) * mm, "end": v(28, -10.79) * mm});
            skLineSegment(sketch, "E18.2.176.0", {"start": v(27.98, -10.81) * mm, "end": v(29.2, -11.68) * mm});
            skLineSegment(sketch, "E18.3.176.0", {"start": v(29.2, -11.68) * mm, "end": v(27.72, -11.46) * mm});
            skLineSegment(sketch, "E18.2.177.0", {"start": v(27.71, -11.49) * mm, "end": v(28.92, -12.38) * mm});
            skLineSegment(sketch, "E18.3.177.0", {"start": v(28.92, -12.38) * mm, "end": v(27.44, -12.13) * mm});
            skLineSegment(sketch, "E18.2.178.0", {"start": v(27.43, -12.16) * mm, "end": v(28.6, -13.08) * mm});
            skLineSegment(sketch, "E18.3.178.0", {"start": v(28.6, -13.08) * mm, "end": v(27.14, -12.8) * mm});
            skLineSegment(sketch, "E18.2.179.0", {"start": v(27.12, -12.82) * mm, "end": v(28.28, -13.77) * mm});
            skLineSegment(sketch, "E18.3.179.0", {"start": v(28.28, -13.77) * mm, "end": v(26.82, -13.45) * mm});
            skLineSegment(sketch, "E19.2.180.0", {"start": v(26.8, -13.47) * mm, "end": v(27.94, -14.45) * mm});
            skLineSegment(sketch, "E19.3.180.0", {"start": v(27.94, -14.45) * mm, "end": v(26.48, -14.1) * mm});
            skLineSegment(sketch, "E19.2.181.0", {"start": v(26.47, -14.12) * mm, "end": v(27.58, -15.13) * mm});
            skLineSegment(sketch, "E19.3.181.0", {"start": v(27.58, -15.13) * mm, "end": v(26.13, -14.73) * mm});
            skLineSegment(sketch, "E19.2.182.0", {"start": v(26.12, -14.76) * mm, "end": v(27.2, -15.8) * mm});
            skLineSegment(sketch, "E19.3.182.0", {"start": v(27.2, -15.8) * mm, "end": v(25.77, -15.36) * mm});
            skLineSegment(sketch, "E19.2.183.0", {"start": v(25.75, -15.39) * mm, "end": v(26.82, -16.45) * mm});
            skLineSegment(sketch, "E19.3.183.0", {"start": v(26.82, -16.45) * mm, "end": v(25.39, -15.98) * mm});
            skLineSegment(sketch, "E19.2.184.0", {"start": v(25.37, -16) * mm, "end": v(26.4, -17.1) * mm});
            skLineSegment(sketch, "E19.3.184.0", {"start": v(26.4, -17.1) * mm, "end": v(25, -16.6) * mm});
            skLineSegment(sketch, "E19.2.185.0", {"start": v(24.98, -16.62) * mm, "end": v(25.99, -17.73) * mm});
            skLineSegment(sketch, "E19.3.185.0", {"start": v(25.99, -17.73) * mm, "end": v(24.58, -17.2) * mm});
            skLineSegment(sketch, "E19.2.186.0", {"start": v(24.57, -17.22) * mm, "end": v(25.55, -18.35) * mm});
            skLineSegment(sketch, "E19.3.186.0", {"start": v(25.55, -18.35) * mm, "end": v(24.16, -17.79) * mm});
            skLineSegment(sketch, "E19.2.187.0", {"start": v(24.14, -17.8) * mm, "end": v(25.1, -18.97) * mm});
            skLineSegment(sketch, "E19.3.187.0", {"start": v(25.1, -18.97) * mm, "end": v(23.72, -18.37) * mm});
            skLineSegment(sketch, "E19.2.188.0", {"start": v(23.7, -18.39) * mm, "end": v(24.63, -19.57) * mm});
            skLineSegment(sketch, "E19.3.188.0", {"start": v(24.63, -19.57) * mm, "end": v(23.27, -18.94) * mm});
            skLineSegment(sketch, "E19.2.189.0", {"start": v(23.25, -18.96) * mm, "end": v(24.15, -20.16) * mm});
            skLineSegment(sketch, "E19.3.189.0", {"start": v(24.15, -20.16) * mm, "end": v(22.8, -19.5) * mm});
            skLineSegment(sketch, "E19.2.190.0", {"start": v(22.78, -19.52) * mm, "end": v(23.65, -20.74) * mm});
            skLineSegment(sketch, "E19.3.190.0", {"start": v(23.65, -20.74) * mm, "end": v(22.32, -20.04) * mm});
            skLineSegment(sketch, "E19.2.191.0", {"start": v(22.3, -20.06) * mm, "end": v(23.14, -21.3) * mm});
            skLineSegment(sketch, "E19.3.191.0", {"start": v(23.14, -21.3) * mm, "end": v(21.83, -20.58) * mm});
            skLineSegment(sketch, "E19.2.192.0", {"start": v(21.81, -20.6) * mm, "end": v(22.62, -21.86) * mm});
            skLineSegment(sketch, "E19.3.192.0", {"start": v(22.62, -21.86) * mm, "end": v(21.32, -21.1) * mm});
            skLineSegment(sketch, "E19.2.193.0", {"start": v(21.3, -21.12) * mm, "end": v(22.08, -22.4) * mm});
            skLineSegment(sketch, "E19.3.193.0", {"start": v(22.08, -22.4) * mm, "end": v(20.8, -21.61) * mm});
            skLineSegment(sketch, "E19.2.194.0", {"start": v(20.79, -21.63) * mm, "end": v(21.53, -22.93) * mm});
            skLineSegment(sketch, "E19.3.194.0", {"start": v(21.53, -22.93) * mm, "end": v(20.28, -22.11) * mm});
            skLineSegment(sketch, "E19.2.195.0", {"start": v(20.26, -22.13) * mm, "end": v(20.97, -23.45) * mm});
            skLineSegment(sketch, "E19.3.195.0", {"start": v(20.97, -23.45) * mm, "end": v(19.73, -22.6) * mm});
            skLineSegment(sketch, "E19.2.196.0", {"start": v(19.71, -22.61) * mm, "end": v(20.4, -23.95) * mm});
            skLineSegment(sketch, "E19.3.196.0", {"start": v(20.4, -23.95) * mm, "end": v(19.18, -23.07) * mm});
            skLineSegment(sketch, "E19.2.197.0", {"start": v(19.16, -23.09) * mm, "end": v(19.8, -24.44) * mm});
            skLineSegment(sketch, "E19.3.197.0", {"start": v(19.8, -24.44) * mm, "end": v(18.61, -23.53) * mm});
            skLineSegment(sketch, "E19.2.198.0", {"start": v(18.6, -23.54) * mm, "end": v(19.2, -24.91) * mm});
            skLineSegment(sketch, "E19.3.198.0", {"start": v(19.2, -24.91) * mm, "end": v(18.04, -23.97) * mm});
            skLineSegment(sketch, "E19.2.199.0", {"start": v(18.02, -23.99) * mm, "end": v(18.6, -25.37) * mm});
            skLineSegment(sketch, "E19.3.199.0", {"start": v(18.6, -25.37) * mm, "end": v(17.45, -24.4) * mm});
            skLineSegment(sketch, "E20.2.200.0", {"start": v(17.43, -24.42) * mm, "end": v(17.98, -25.81) * mm});
            skLineSegment(sketch, "E20.3.200.0", {"start": v(17.98, -25.81) * mm, "end": v(16.85, -24.82) * mm});
            skLineSegment(sketch, "E20.2.201.0", {"start": v(16.83, -24.83) * mm, "end": v(17.34, -26.24) * mm});
            skLineSegment(sketch, "E20.3.201.0", {"start": v(17.34, -26.24) * mm, "end": v(16.25, -25.22) * mm});
            skLineSegment(sketch, "E20.2.202.0", {"start": v(16.22, -25.23) * mm, "end": v(16.7, -26.66) * mm});
            skLineSegment(sketch, "E20.3.202.0", {"start": v(16.7, -26.66) * mm, "end": v(15.63, -25.6) * mm});
            skLineSegment(sketch, "E20.2.203.0", {"start": v(15.6, -25.62) * mm, "end": v(16.05, -27.05) * mm});
            skLineSegment(sketch, "E20.3.203.0", {"start": v(16.05, -27.05) * mm, "end": v(15, -25.98) * mm});
            skLineSegment(sketch, "E20.2.204.0", {"start": v(14.98, -26) * mm, "end": v(15.39, -27.43) * mm});
            skLineSegment(sketch, "E20.3.204.0", {"start": v(15.39, -27.43) * mm, "end": v(14.37, -26.33) * mm});
            skLineSegment(sketch, "E20.2.205.0", {"start": v(14.35, -26.35) * mm, "end": v(14.72, -27.8) * mm});
            skLineSegment(sketch, "E20.3.205.0", {"start": v(14.72, -27.8) * mm, "end": v(13.73, -26.67) * mm});
            skLineSegment(sketch, "E20.2.206.0", {"start": v(13.7, -26.69) * mm, "end": v(14.04, -28.15) * mm});
            skLineSegment(sketch, "E20.3.206.0", {"start": v(14.04, -28.15) * mm, "end": v(13.08, -27) * mm});
            skLineSegment(sketch, "E20.2.207.0", {"start": v(13.05, -27.01) * mm, "end": v(13.35, -28.48) * mm});
            skLineSegment(sketch, "E20.3.207.0", {"start": v(13.35, -28.48) * mm, "end": v(12.42, -27.3) * mm});
            skLineSegment(sketch, "E20.2.208.0", {"start": v(12.4, -27.32) * mm, "end": v(12.66, -28.8) * mm});
            skLineSegment(sketch, "E20.3.208.0", {"start": v(12.66, -28.8) * mm, "end": v(11.75, -27.6) * mm});
            skLineSegment(sketch, "E20.2.209.0", {"start": v(11.73, -27.61) * mm, "end": v(11.96, -29.1) * mm});
            skLineSegment(sketch, "E20.3.209.0", {"start": v(11.96, -29.1) * mm, "end": v(11.08, -27.88) * mm});
            skLineSegment(sketch, "E20.2.210.0", {"start": v(11.05, -27.89) * mm, "end": v(11.25, -29.38) * mm});
            skLineSegment(sketch, "E20.3.210.0", {"start": v(11.25, -29.38) * mm, "end": v(10.4, -28.14) * mm});
            skLineSegment(sketch, "E20.2.211.0", {"start": v(10.37, -28.15) * mm, "end": v(10.53, -29.64) * mm});
            skLineSegment(sketch, "E20.3.211.0", {"start": v(10.53, -29.64) * mm, "end": v(9.71, -28.38) * mm});
            skLineSegment(sketch, "E20.2.212.0", {"start": v(9.69, -28.4) * mm, "end": v(9.8, -29.89) * mm});
            skLineSegment(sketch, "E20.3.212.0", {"start": v(9.8, -29.89) * mm, "end": v(9.02, -28.61) * mm});
            skLineSegment(sketch, "E20.2.213.0", {"start": v(9, -28.62) * mm, "end": v(9.08, -30.12) * mm});
            skLineSegment(sketch, "E20.3.213.0", {"start": v(9.08, -30.12) * mm, "end": v(8.33, -28.82) * mm});
            skLineSegment(sketch, "E20.2.214.0", {"start": v(8.3, -28.83) * mm, "end": v(8.35, -30.33) * mm});
            skLineSegment(sketch, "E20.3.214.0", {"start": v(8.35, -30.33) * mm, "end": v(7.62, -29.01) * mm});
            skLineSegment(sketch, "E20.2.215.0", {"start": v(7.6, -29.02) * mm, "end": v(7.61, -30.52) * mm});
            skLineSegment(sketch, "E20.3.215.0", {"start": v(7.61, -30.52) * mm, "end": v(6.92, -29.2) * mm});
            skLineSegment(sketch, "E20.2.216.0", {"start": v(6.9, -29.2) * mm, "end": v(6.87, -30.7) * mm});
            skLineSegment(sketch, "E20.3.216.0", {"start": v(6.87, -30.7) * mm, "end": v(6.2, -29.35) * mm});
            skLineSegment(sketch, "E20.2.217.0", {"start": v(6.18, -29.36) * mm, "end": v(6.12, -30.86) * mm});
            skLineSegment(sketch, "E20.3.217.0", {"start": v(6.12, -30.86) * mm, "end": v(5.5, -29.5) * mm});
            skLineSegment(sketch, "E20.2.218.0", {"start": v(5.47, -29.5) * mm, "end": v(5.37, -31) * mm});
            skLineSegment(sketch, "E20.3.218.0", {"start": v(5.37, -31) * mm, "end": v(4.78, -29.62) * mm});
            skLineSegment(sketch, "E20.2.219.0", {"start": v(4.75, -29.62) * mm, "end": v(4.62, -31.12) * mm});
            skLineSegment(sketch, "E20.3.219.0", {"start": v(4.62, -31.12) * mm, "end": v(4.06, -29.72) * mm});
            skLineSegment(sketch, "E21.2.220.0", {"start": v(4.03, -29.73) * mm, "end": v(3.86, -31.22) * mm});
            skLineSegment(sketch, "E21.3.220.0", {"start": v(3.86, -31.22) * mm, "end": v(3.34, -29.81) * mm});
            skLineSegment(sketch, "E21.2.221.0", {"start": v(3.3, -29.82) * mm, "end": v(3.1, -31.3) * mm});
            skLineSegment(sketch, "E21.3.221.0", {"start": v(3.1, -31.3) * mm, "end": v(2.61, -29.89) * mm});
            skLineSegment(sketch, "E21.2.222.0", {"start": v(2.58, -29.89) * mm, "end": v(2.34, -31.37) * mm});
            skLineSegment(sketch, "E21.3.222.0", {"start": v(2.34, -31.37) * mm, "end": v(1.89, -29.94) * mm});
            skLineSegment(sketch, "E21.2.223.0", {"start": v(1.86, -29.94) * mm, "end": v(1.58, -31.42) * mm});
            skLineSegment(sketch, "E21.3.223.0", {"start": v(1.58, -31.42) * mm, "end": v(1.16, -29.98) * mm});
            skLineSegment(sketch, "E21.2.224.0", {"start": v(1.13, -29.98) * mm, "end": v(0.82, -31.45) * mm});
            skLineSegment(sketch, "E21.3.224.0", {"start": v(0.82, -31.45) * mm, "end": v(0.43, -30) * mm});
            skLineSegment(sketch, "E21.2.225.0", {"start": v(0.4, -30) * mm, "end": v(0.06, -31.46) * mm});
            skLineSegment(sketch, "E21.3.225.0", {"start": v(0.06, -31.46) * mm, "end": v(-0.3, -30) * mm});
            skLineSegment(sketch, "E21.2.226.0", {"start": v(-0.32, -30) * mm, "end": v(-0.7, -31.45) * mm});
            skLineSegment(sketch, "E21.3.226.0", {"start": v(-0.7, -31.45) * mm, "end": v(-1.02, -29.98) * mm});
            skLineSegment(sketch, "E21.2.227.0", {"start": v(-1.05, -29.98) * mm, "end": v(-1.47, -31.42) * mm});
            skLineSegment(sketch, "E21.3.227.0", {"start": v(-1.47, -31.42) * mm, "end": v(-1.75, -29.95) * mm});
            skLineSegment(sketch, "E21.2.228.0", {"start": v(-1.78, -29.95) * mm, "end": v(-2.23, -31.38) * mm});
            skLineSegment(sketch, "E21.3.228.0", {"start": v(-2.23, -31.38) * mm, "end": v(-2.48, -29.9) * mm});
            skLineSegment(sketch, "E21.2.229.0", {"start": v(-2.5, -29.9) * mm, "end": v(-3, -31.31) * mm});
            skLineSegment(sketch, "E21.3.229.0", {"start": v(-3, -31.31) * mm, "end": v(-3.2, -29.83) * mm});
            skLineSegment(sketch, "E22.2.230.0", {"start": v(-3.23, -29.83) * mm, "end": v(-3.75, -31.23) * mm});
            skLineSegment(sketch, "E22.3.230.0", {"start": v(-3.75, -31.23) * mm, "end": v(-3.92, -29.74) * mm});
            skLineSegment(sketch, "E22.2.231.0", {"start": v(-3.95, -29.74) * mm, "end": v(-4.5, -31.13) * mm});
            skLineSegment(sketch, "E22.3.231.0", {"start": v(-4.5, -31.13) * mm, "end": v(-4.64, -29.64) * mm});
            skLineSegment(sketch, "E22.2.232.0", {"start": v(-4.67, -29.63) * mm, "end": v(-5.26, -31.01) * mm});
            skLineSegment(sketch, "E22.3.232.0", {"start": v(-5.26, -31.01) * mm, "end": v(-5.36, -29.52) * mm});
            skLineSegment(sketch, "E22.2.233.0", {"start": v(-5.39, -29.51) * mm, "end": v(-6.01, -30.88) * mm});
            skLineSegment(sketch, "E22.3.233.0", {"start": v(-6.01, -30.88) * mm, "end": v(-6.08, -29.38) * mm});
            skLineSegment(sketch, "E22.2.234.0", {"start": v(-6.1, -29.37) * mm, "end": v(-6.76, -30.72) * mm});
            skLineSegment(sketch, "E22.3.234.0", {"start": v(-6.76, -30.72) * mm, "end": v(-6.79, -29.22) * mm});
            skLineSegment(sketch, "E22.2.235.0", {"start": v(-6.81, -29.22) * mm, "end": v(-7.5, -30.55) * mm});
            skLineSegment(sketch, "E22.3.235.0", {"start": v(-7.5, -30.55) * mm, "end": v(-7.5, -29.05) * mm});
            skLineSegment(sketch, "E22.2.236.0", {"start": v(-7.52, -29.04) * mm, "end": v(-8.24, -30.36) * mm});
            skLineSegment(sketch, "E22.3.236.0", {"start": v(-8.24, -30.36) * mm, "end": v(-8.2, -28.86) * mm});
            skLineSegment(sketch, "E22.2.237.0", {"start": v(-8.22, -28.85) * mm, "end": v(-8.97, -30.15) * mm});
            skLineSegment(sketch, "E22.3.237.0", {"start": v(-8.97, -30.15) * mm, "end": v(-8.9, -28.65) * mm});
            skLineSegment(sketch, "E22.2.238.0", {"start": v(-8.92, -28.64) * mm, "end": v(-9.7, -29.92) * mm});
            skLineSegment(sketch, "E22.3.238.0", {"start": v(-9.7, -29.92) * mm, "end": v(-9.59, -28.43) * mm});
            skLineSegment(sketch, "E22.2.239.0", {"start": v(-9.61, -28.42) * mm, "end": v(-10.43, -29.68) * mm});
            skLineSegment(sketch, "E22.3.239.0", {"start": v(-10.43, -29.68) * mm, "end": v(-10.27, -28.19) * mm});
            skLineSegment(sketch, "E22.2.240.0", {"start": v(-10.3, -28.18) * mm, "end": v(-11.14, -29.42) * mm});
            skLineSegment(sketch, "E22.3.240.0", {"start": v(-11.14, -29.42) * mm, "end": v(-10.95, -27.93) * mm});
            skLineSegment(sketch, "E22.2.241.0", {"start": v(-10.98, -27.92) * mm, "end": v(-11.85, -29.14) * mm});
            skLineSegment(sketch, "E22.3.241.0", {"start": v(-11.85, -29.14) * mm, "end": v(-11.63, -27.65) * mm});
            skLineSegment(sketch, "E22.2.242.0", {"start": v(-11.65, -27.64) * mm, "end": v(-12.56, -28.84) * mm});
            skLineSegment(sketch, "E22.3.242.0", {"start": v(-12.56, -28.84) * mm, "end": v(-12.3, -27.36) * mm});
            skLineSegment(sketch, "E22.2.243.0", {"start": v(-12.32, -27.35) * mm, "end": v(-13.25, -28.53) * mm});
            skLineSegment(sketch, "E22.3.243.0", {"start": v(-13.25, -28.53) * mm, "end": v(-12.96, -27.06) * mm});
            skLineSegment(sketch, "E22.2.244.0", {"start": v(-12.98, -27.05) * mm, "end": v(-13.94, -28.2) * mm});
            skLineSegment(sketch, "E22.3.244.0", {"start": v(-13.94, -28.2) * mm, "end": v(-13.6, -26.74) * mm});
            skLineSegment(sketch, "E22.2.245.0", {"start": v(-13.63, -26.72) * mm, "end": v(-14.62, -27.85) * mm});
            skLineSegment(sketch, "E22.3.245.0", {"start": v(-14.62, -27.85) * mm, "end": v(-14.25, -26.4) * mm});
            skLineSegment(sketch, "E22.2.246.0", {"start": v(-14.28, -26.38) * mm, "end": v(-15.3, -27.49) * mm});
            skLineSegment(sketch, "E22.3.246.0", {"start": v(-15.3, -27.49) * mm, "end": v(-14.89, -26.04) * mm});
            skLineSegment(sketch, "E22.2.247.0", {"start": v(-14.91, -26.03) * mm, "end": v(-15.95, -27.11) * mm});
            skLineSegment(sketch, "E22.3.247.0", {"start": v(-15.95, -27.11) * mm, "end": v(-15.52, -25.68) * mm});
            skLineSegment(sketch, "E22.2.248.0", {"start": v(-15.54, -25.66) * mm, "end": v(-16.6, -26.72) * mm});
            skLineSegment(sketch, "E22.3.248.0", {"start": v(-16.6, -26.72) * mm, "end": v(-16.13, -25.3) * mm});
            skLineSegment(sketch, "E22.2.249.0", {"start": v(-16.16, -25.28) * mm, "end": v(-17.25, -26.3) * mm});
            skLineSegment(sketch, "E22.3.249.0", {"start": v(-17.25, -26.3) * mm, "end": v(-16.74, -24.9) * mm});
            skLineSegment(sketch, "E23.2.250.0", {"start": v(-16.77, -24.88) * mm, "end": v(-17.88, -25.88) * mm});
            skLineSegment(sketch, "E23.3.250.0", {"start": v(-17.88, -25.88) * mm, "end": v(-17.34, -24.48) * mm});
            skLineSegment(sketch, "E23.2.251.0", {"start": v(-17.36, -24.46) * mm, "end": v(-18.5, -25.44) * mm});
            skLineSegment(sketch, "E23.3.251.0", {"start": v(-18.5, -25.44) * mm, "end": v(-17.93, -24.05) * mm});
            skLineSegment(sketch, "E23.2.252.0", {"start": v(-17.95, -24.04) * mm, "end": v(-19.12, -24.98) * mm});
            skLineSegment(sketch, "E23.3.252.0", {"start": v(-19.12, -24.98) * mm, "end": v(-18.5, -23.6) * mm});
            skLineSegment(sketch, "E23.2.253.0", {"start": v(-18.53, -23.6) * mm, "end": v(-19.72, -24.5) * mm});
            skLineSegment(sketch, "E23.3.253.0", {"start": v(-19.72, -24.5) * mm, "end": v(-19.08, -23.15) * mm});
            skLineSegment(sketch, "E23.2.254.0", {"start": v(-19.1, -23.14) * mm, "end": v(-20.3, -24.02) * mm});
            skLineSegment(sketch, "E23.3.254.0", {"start": v(-20.3, -24.02) * mm, "end": v(-19.63, -22.68) * mm});
            skLineSegment(sketch, "E23.2.255.0", {"start": v(-19.65, -22.67) * mm, "end": v(-20.88, -23.52) * mm});
            skLineSegment(sketch, "E23.3.255.0", {"start": v(-20.88, -23.52) * mm, "end": v(-20.18, -22.2) * mm});
            skLineSegment(sketch, "E23.2.256.0", {"start": v(-20.2, -22.18) * mm, "end": v(-21.45, -23.01) * mm});
            skLineSegment(sketch, "E23.3.256.0", {"start": v(-21.45, -23.01) * mm, "end": v(-20.7, -21.7) * mm});
            skLineSegment(sketch, "E23.2.257.0", {"start": v(-20.73, -21.69) * mm, "end": v(-22, -22.48) * mm});
            skLineSegment(sketch, "E23.3.257.0", {"start": v(-22, -22.48) * mm, "end": v(-21.23, -21.2) * mm});
            skLineSegment(sketch, "E23.2.258.0", {"start": v(-21.25, -21.18) * mm, "end": v(-22.54, -21.94) * mm});
            skLineSegment(sketch, "E23.3.258.0", {"start": v(-22.54, -21.94) * mm, "end": v(-21.74, -20.68) * mm});
            skLineSegment(sketch, "E23.2.259.0", {"start": v(-21.76, -20.66) * mm, "end": v(-23.06, -21.4) * mm});
            skLineSegment(sketch, "E23.3.259.0", {"start": v(-23.06, -21.4) * mm, "end": v(-22.23, -20.14) * mm});
            skSolve(sketch);
        }
        {
            var Q0;
            Q0 = qSketchRegion(id + "F0", true);
            extrude(context, id + "F1", {"entities" : qUnion([Q0]), "depth" : 10 * mm});
        }
        {
            var Q0;
            Q0 = qSketchRegion(id + "F0", true);
            extrude(context, id + "F2", {"entities" : qUnion([Q0]), "operationType" : NewBodyOperationType.ADD, "depth" : 25 * mm});
        }
    });
